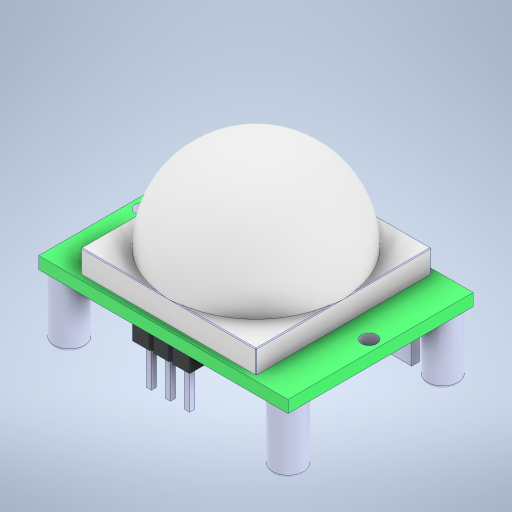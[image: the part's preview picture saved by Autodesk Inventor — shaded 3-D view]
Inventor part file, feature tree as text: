
AUTODESK INVENTOR PART (.ipt)
format: ipt  version: 2024 (Build 280153000, 153)  size: 449,536 bytes
history: native  units: mm
features: extrude x1
ambient origin geometry x8: Origin, YZ Plane, XZ Plane, XY Plane, X Axis, Y Axis, Z Axis, Center Point
bodies: Solid1 (feature_tree)
feature tree (1):
  extrude  "Extrude11"  [1 undecoded]
note: 1 required parameter value undecoded (feature->parameter linkage not recoverable at this tier; creation-order binding heuristic only, values carry confidence <= 0.55)
